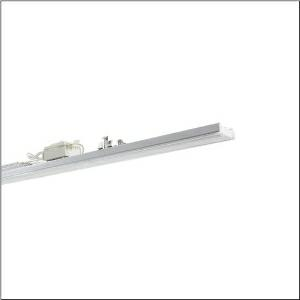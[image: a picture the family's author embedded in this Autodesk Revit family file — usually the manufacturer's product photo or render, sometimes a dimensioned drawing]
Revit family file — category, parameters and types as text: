
# Revit family: licross_r__11_recessed_mo_51te12dn4axg_6a97
name_source: partatom
category: Lighting Fixtures
units: mm (PartAtom-declared; Revit-internal decimal feet)

## family parameters
Cut with Voids When Loaded = No
Host = Face
Light Source = No
Part Type = Normal
Room Calculation Point = No
Round Connector Dimension = Use Diameter
Shared = No

## types (1)
- --- (1 x LED, 10240 lm, 56.7 W, 4000K)
    Apparent Load = 57 VA
    CIE Flux Codes = 67 92 99 100 100
    Color Rendering = 80
    Color Temperature = 4000K
    Default Elevation = 1800 mm
    Description = Licross® 11 Recessed MO, luminaire insert, of sheet steel, galvanised, coil coated, white, length: 1.500mm, width: 66mm, height: 67mm, LED rated luminous flux: 10.240lm, light colour: 840, control gear: DALI 2, with plug, 5-pole, with phase selection, mains connection: 220..240V, AC, 50/60Hz, rated input power: 57W, internal wiring halogen-free, primary optical cover: cover, of PMMA, light emission: direct distribution, primary light characteristic: symmetric, protection rating (complete): IP54, insulation class (complete): insulation class I (protective earthing), certification: CE, ENEC, VDE, UKCA, protection symbol: D if used in an environment with non-conductive dust loads with corresponding accessories, impact resistance: IK06, permissible ambient temperature for indoor applications: -25..+35°C, corresponds to IFS (International Featured Standards) requirements for safety and quality in the food industry, reducing of maximum allowable ambient temperature of 5°C with ceiling mounting, LABS conformity tested according to VDMA 24364:2018-05, packaging unit: 1 piece
    Height = 58 mm
    Lamp = 1 x LED
    Lamp Light Flux = 10240 lm
    Lamp Power = 56.7 W
    Lamp count = 1
    Length = 1500 mm
    Luminous efficacy = 181 lm/W
    Manufacturer = Siteco
    ModVariant = No
    Model = 51TE12DN4AXG
    Mounting Place = Ceiling
    Mounting Type = Pendant
    Number of Poles = 1
    OnlyDefault = Yes
    Power Factor = 1
    Product Name = Licross® 11 Recessed MO
    Product group = luminaire insert | ceiling pendant
    ProductGroupID = 902
    Protection Class = Protection class I
    Protection Degree = IP 54
    RLX_Detail_Level = 1
    RLX_Emergency_Light_Flux = 0 lm
    RLX_Emergency_Type = 0
    RLX_Emergency_Type_DB = No
    RlxData = <blob elided: 24477 chars, md5=d274e424>
    Socket = socket
    Standby Power = 0 W
    System Light Flux = 10240 lm
    System Power = 57 W
    Type Comments = factory setting: luminous flux: 100 % | dim-lin: 254 | 378 mA
    Type Image = l_1296930.jpg
    URL = http://relux.com
    VarID = @adj_121661
    Voltage = 0 V
    Weight = 0.00 kg
    Width = 66 mm

## geometry (parser evidence)
native form markers: Blend x4, Sweep x9
no freeform markers — native parametric forms only
